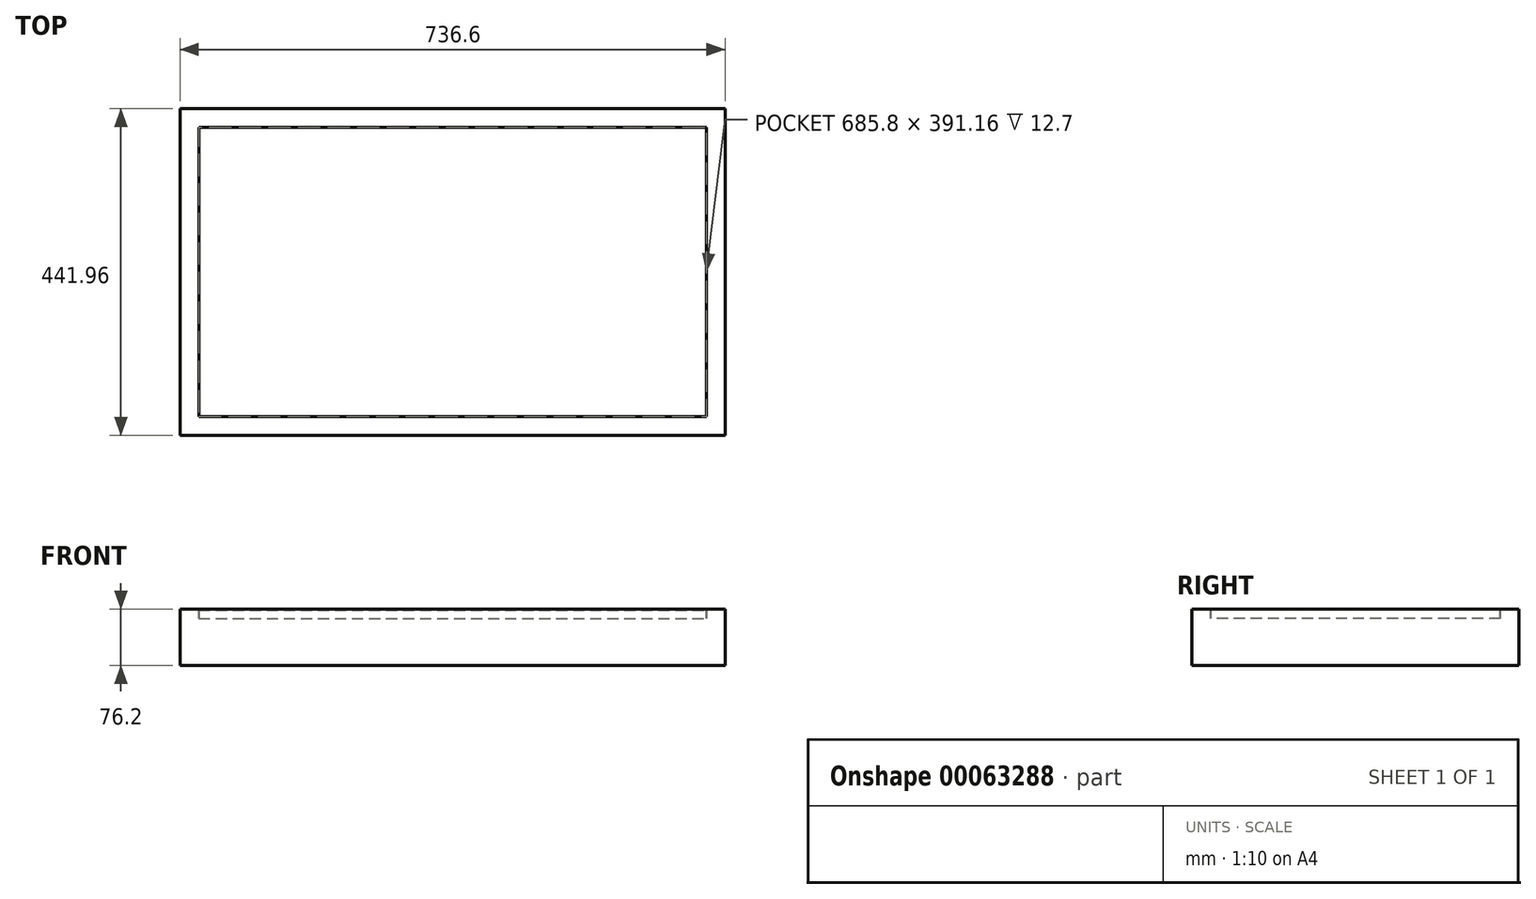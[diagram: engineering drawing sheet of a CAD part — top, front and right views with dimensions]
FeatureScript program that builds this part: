
annotation { "Feature Type Name" : "Feature", "Feature Type Description" : "" }
export const myFeature = defineFeature(function(context is Context, id is Id, definition is map)
    precondition{}
    {
        {
            assignVariable(context, id + "F0", {"name" : "TVDepth", "anyValue" : 76.2 * mm});
        }
        {
            var Q0;
            Q0=qCreatedBy(makeId("Top.planeOp"),FACE);
            var sketch = newSketch(context, id + "F1", { "sketchPlane" : qUnion([Q0])});
            skLineSegment(sketch, "E0.bottom", {"start": v(-368.3, -220.98) * mm, "end": v(368.3, -220.98) * mm});
            skLineSegment(sketch, "E0.top", {"start": v(-368.3, 220.98) * mm, "end": v(368.3, 220.98) * mm});
            skLineSegment(sketch, "E0.left", {"start": v(-368.3, -220.98) * mm, "end": v(-368.3, 220.98) * mm});
            skLineSegment(sketch, "E0.right", {"start": v(368.3, -220.98) * mm, "end": v(368.3, 220.98) * mm});
            skPoint(sketch, "E1.endSnap0", {"position": v(0, -220.98) * mm});
            skLineSegment(sketch, "E2", {"start": v(-368.3, 0) * mm, "end": v(368.3, 0) * mm, "construction": true});
            skLineSegment(sketch, "E3", {"start": v(0, -220.98) * mm, "end": v(0, 220.98) * mm, "construction": true});
            skSolve(sketch);
        }
        {
            var Q0;
            Q0 = qSketchRegion(id + "F1", true);
            extrude(context, id + "F2", {"entities" : qUnion([Q0]), "depth" : getVariable(context, 'TVDepth')});
        }
        {
            var Q0;
            Q0=makeQuery(id+"F2.opExtrude","CAP_FACE",FACE,{"disambiguationData":[OSD([sQuery(id+"F1.wireOp",EDGE,"E0.bottom"),sQuery(id+"F1.wireOp",EDGE,"E0.top"),sQuery(id+"F1.wireOp",EDGE,"E0.left"),sQuery(id+"F1.wireOp",EDGE,"E0.right")])],"isStart":false});
            var sketch = newSketch(context, id + "F3", { "sketchPlane" : qUnion([Q0])});
            skLineSegment(sketch, "E4.bottom", {"start": v(-342.9, 195.58) * mm, "end": v(342.9, 195.58) * mm});
            skLineSegment(sketch, "E4.top", {"start": v(-342.9, -195.58) * mm, "end": v(342.9, -195.58) * mm});
            skLineSegment(sketch, "E4.left", {"start": v(-342.9, 195.58) * mm, "end": v(-342.9, -195.58) * mm});
            skLineSegment(sketch, "E4.right", {"start": v(342.9, 195.58) * mm, "end": v(342.9, -195.58) * mm});
            skSolve(sketch);
        }
        {
            var Q0;
            Q0 = qSketchRegion(id + "F3", true);
            extrude(context, id + "F4", {"entities" : qUnion([Q0]), "operationType" : NewBodyOperationType.REMOVE, "oppositeDirection" : true, "depth" : 12.7 * mm});
        }
        {
            var Q0;
            Q0=makeQuery(id+"F4.boolean.opBoolean","COPY",FACE,{"derivedFrom":makeQuery(id+"F4.opExtrude","CAP_FACE",FACE,{"disambiguationData":[OSD([sQuery(id+"F3.wireOp",EDGE,"E4.bottom"),sQuery(id+"F3.wireOp",EDGE,"E4.top"),sQuery(id+"F3.wireOp",EDGE,"E4.left"),sQuery(id+"F3.wireOp",EDGE,"E4.right")])],"isStart":false})});
            var sketch = newSketch(context, id + "F5", { "sketchPlane" : qUnion([Q0])});
            skLineSegment(sketch, "E5.bottom", {"start": v(-342.9, 195.58) * mm, "end": v(342.9, 195.58) * mm});
            skLineSegment(sketch, "E5.top", {"start": v(-342.9, -195.58) * mm, "end": v(342.9, -195.58) * mm});
            skLineSegment(sketch, "E5.left", {"start": v(-342.9, 195.58) * mm, "end": v(-342.9, -195.58) * mm});
            skLineSegment(sketch, "E5.right", {"start": v(342.9, 195.58) * mm, "end": v(342.9, -195.58) * mm});
            skSolve(sketch);
        }
        {
            var Q0;
            Q0 = qSketchRegion(id + "F5", true);
            extrude(context, id + "F6", {"entities" : qUnion([Q0]), "depth" : 11.43 * mm});
        }
    });
